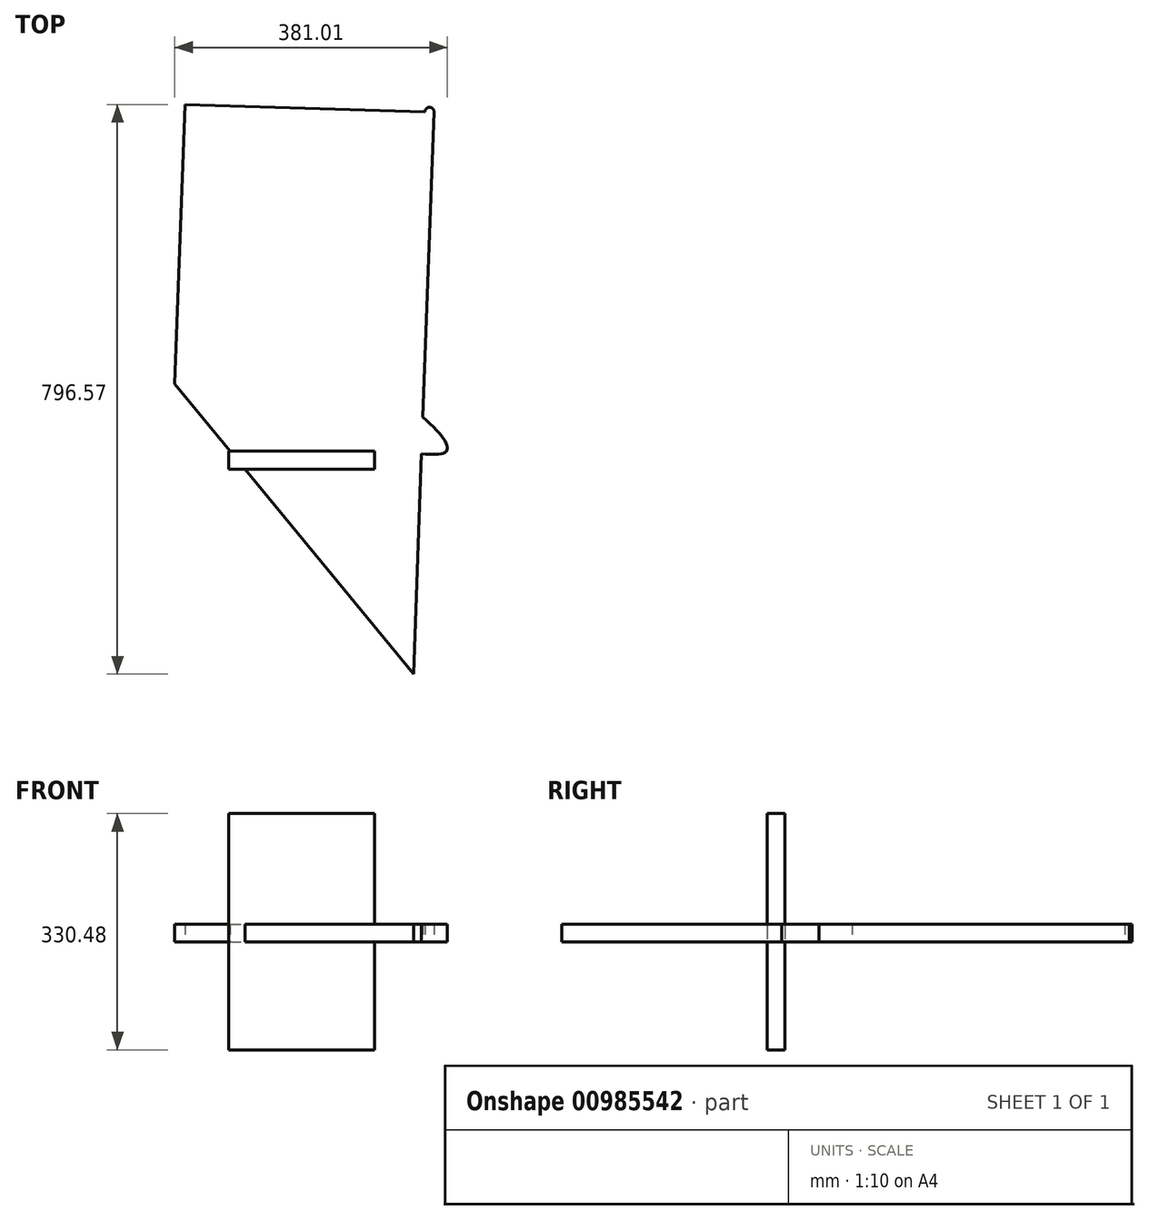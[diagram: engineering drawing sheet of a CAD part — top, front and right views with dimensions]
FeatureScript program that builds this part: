
annotation { "Feature Type Name" : "Feature", "Feature Type Description" : "" }
export const myFeature = defineFeature(function(context is Context, id is Id, definition is map)
    precondition{}
    {
        {
            var Q0;
            Q0=qCreatedBy(makeId("Front.planeOp"),FACE);
            var sketch = newSketch(context, id + "F0", { "sketchPlane" : qUnion([Q0])});
            skLineSegment(sketch, "E0.bottom", {"start": v(410, -325) * mm, "end": v(-410, -325) * mm});
            skLineSegment(sketch, "E0.top", {"start": v(410, 325) * mm, "end": v(-410, 325) * mm});
            skLineSegment(sketch, "E0.left", {"start": v(410, -325) * mm, "end": v(410, 325) * mm});
            skLineSegment(sketch, "E0.right", {"start": v(-410, -325) * mm, "end": v(-410, 325) * mm});
            skPoint(sketch, "E0.middle", {"position": v(0, 0) * mm});
            skSolve(sketch);
        }
        {
            var Q0;
            Q0=qCreatedBy(makeId("Top.planeOp"),FACE);
            var sketch = newSketch(context, id + "F1", { "sketchPlane" : qUnion([Q0])});
            skLineSegment(sketch, "E1", {"start": v(181.04, 474.45) * mm, "end": v(166.64, 81.42) * mm});
            skFitSpline(sketch, "E2", {"points": [v(-312.13, -196.62) * mm, v(-312.01, -228.58) * mm, v(-298.35, 89.02) * mm, v(0, 145) * mm, v(198.2, 0) * mm, v(3.1, 3.13) * mm, v(-147.57, -168.65) * mm]});
            skPoint(sketch, "E3", {"position": v(-88.06, -103.34) * mm});
            skPoint(sketch, "E4", {"position": v(-41.26, -49.38) * mm});
            skPoint(sketch, "E5.visualSharp", {"position": v(168.92, 143.54) * mm});
            skArc(sketch, "E5.filletArc", {"start": v(181.04, 474.45) * mm, "mid": v(170.79, 479.7) * mm, "end": v(173.37, 468.48) * mm});
            skLineSegment(sketch, "E6", {"start": v(166.64, 81.42) * mm, "end": v(159.45, -115.1) * mm});
            skLineSegment(sketch, "E7", {"start": v(159.45, -115.1) * mm, "end": v(155.85, -213.35) * mm});
            skLineSegment(sketch, "E8", {"start": v(155.85, -213.35) * mm, "end": v(152.25, -311.6) * mm});
            skLineSegment(sketch, "E9.0", {"start": v(164.15, 81.52) * mm, "end": v(157, -113.88) * mm});
            skLineSegment(sketch, "E9.1", {"start": v(178.46, 472.32) * mm, "end": v(164.15, 81.52) * mm});
            skLineSegment(sketch, "E10.0", {"start": v(-167, 484.96) * mm, "end": v(-181.3, 94.17) * mm});
            skLineSegment(sketch, "E11", {"start": v(-167, 484.96) * mm, "end": v(181.04, 474.45) * mm});
            skLineSegment(sketch, "E12", {"start": v(-181.3, 94.17) * mm, "end": v(152.25, -311.6) * mm});
            skSolve(sketch);
        }
        {
            var Q0;
            Q0 = qSketchRegion(id + "F1", true);
            extrude(context, id + "F2", {"entities" : qUnion([Q0]), "depth" : 25 * mm, "offsetDistance" : 25 * mm});
        }
        {
            var Q0;
            Q0=makeQuery(id+"F0.imprint","IMPRINT",FACE,{"disambiguationData":[TD([[makeQuery(id+"F0.imprint","IMPRINT",EDGE,{"derivedFrom":sQuery(id+"F0.wireOp",EDGE,"E0.bottom")}),-1.0]])]});
            var sketch = newSketch(context, id + "F3", { "sketchPlane" : qUnion([Q0])});
            skLineSegment(sketch, "E13.bottom", {"start": v(-106.04, 179.57) * mm, "end": v(98.25, 179.57) * mm});
            skLineSegment(sketch, "E13.top", {"start": v(-106.04, -150.91) * mm, "end": v(98.25, -150.91) * mm});
            skLineSegment(sketch, "E13.left", {"start": v(-106.04, 179.57) * mm, "end": v(-106.04, -150.91) * mm});
            skLineSegment(sketch, "E13.right", {"start": v(98.25, 179.57) * mm, "end": v(98.25, -150.91) * mm});
            skSolve(sketch);
        }
        {
            var Q0;
            Q0=makeQuery(id+"F3.imprint","IMPRINT",FACE,{"disambiguationData":[TD([[makeQuery(id+"F3.imprint","IMPRINT",EDGE,{"derivedFrom":sQuery(id+"F3.wireOp",EDGE,"E13.bottom")}),-1.0]])]});
            extrude(context, id + "F4", {"entities" : qUnion([Q0]), "operationType" : NewBodyOperationType.ADD, "depth" : 25 * mm, "offsetDistance" : 25 * mm});
        }
    });
